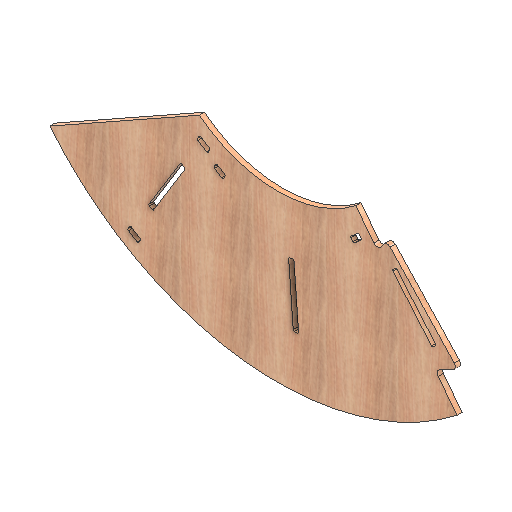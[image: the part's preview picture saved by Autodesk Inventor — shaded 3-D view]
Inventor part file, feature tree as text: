
AUTODESK INVENTOR PART (.ipt)
format: ipt  version: 2021 (Build 250183000, 183)  size: 355,840 bytes
history: native  units: mm
features: other x2, extrude x2, hole x1
ambient origin geometry x8: Origin, YZ Plane, XZ Plane, XY Plane, X Axis, Y Axis, Z Axis, Center Point
bodies: Body1 (feature_tree)
feature tree (5):
  other  "CONTOURS"
  hole  "HOLES"  [1 undecoded]
  other  "LETTERS"
  extrude  "Extrusion2"  Depth=116.345829mm
  extrude  "Extrusion3"  Depth=116.323394mm
note: 1 required parameter value undecoded (feature->parameter linkage not recoverable at this tier; creation-order binding heuristic only, values carry confidence <= 0.55)
